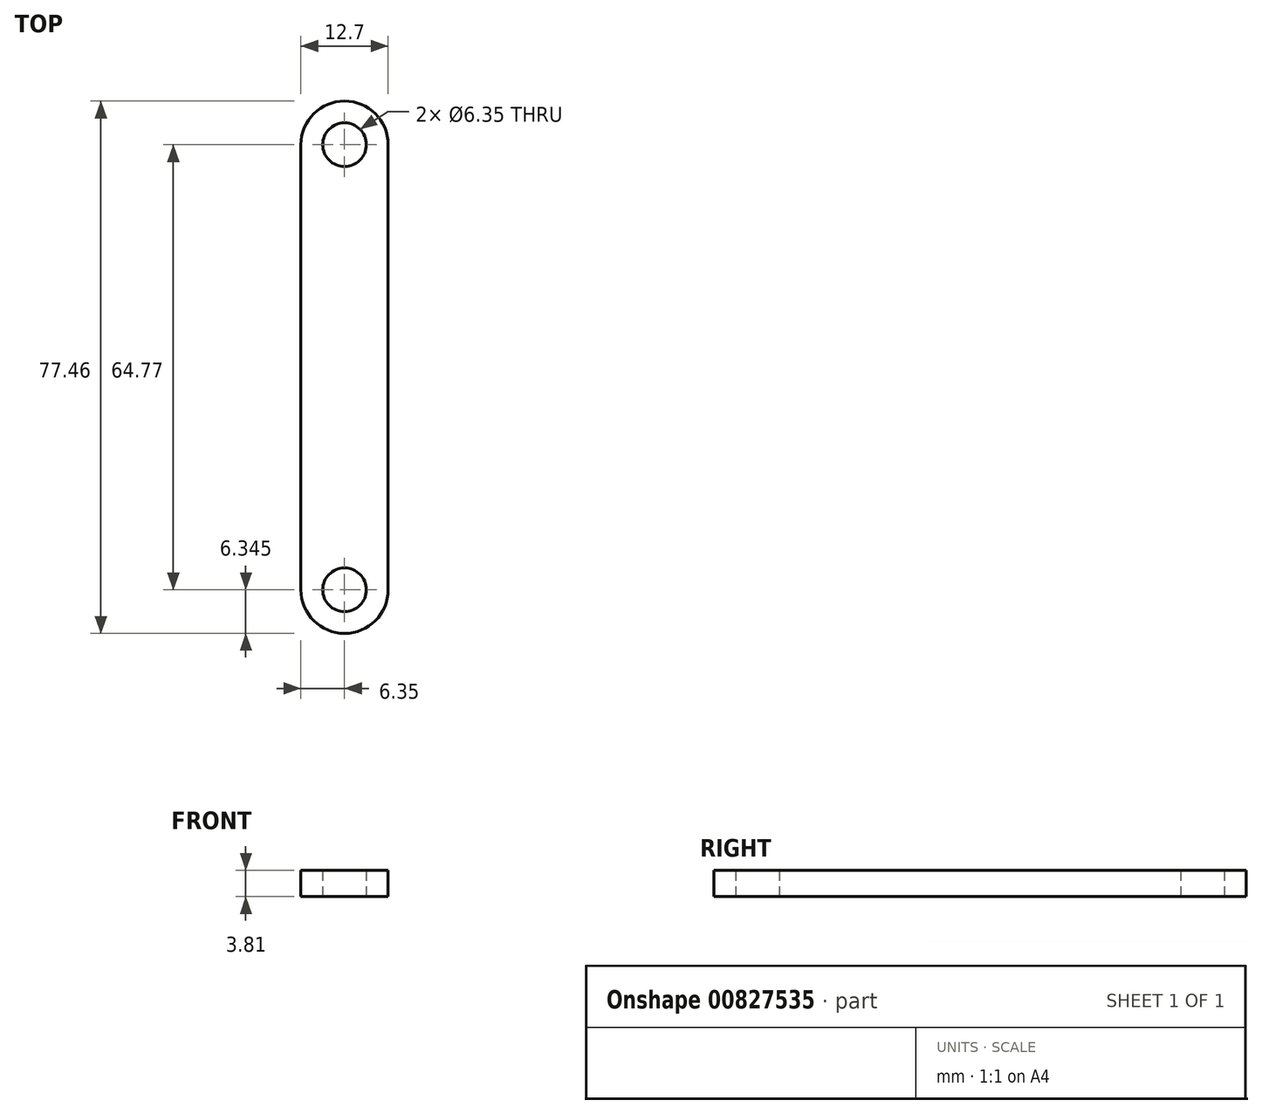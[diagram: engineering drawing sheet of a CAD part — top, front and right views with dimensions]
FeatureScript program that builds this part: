
annotation { "Feature Type Name" : "Feature", "Feature Type Description" : "" }
export const myFeature = defineFeature(function(context is Context, id is Id, definition is map)
    precondition{}
    {
        {
            var Q0;
            Q0=qCreatedBy(makeId("Top.planeOp"),FACE);
            var sketch = newSketch(context, id + "F0", { "sketchPlane" : qUnion([Q0])});
            skCircle(sketch, "E0", {"center": v(0, 32.39) * mm, "radius": 3.18 * mm});
            skCircle(sketch, "E1", {"center": v(0, -32.39) * mm, "radius": 3.18 * mm});
            skLineSegment(sketch, "E2", {"start": v(0, 0) * mm, "end": v(0, 29.21) * mm});
            skLineSegment(sketch, "E3", {"start": v(0, 0) * mm, "end": v(0, -29.21) * mm});
            skLineSegment(sketch, "E4.bottom", {"start": v(-6.35, 32.39) * mm, "end": v(6.35, 32.39) * mm});
            skLineSegment(sketch, "E4.top", {"start": v(-6.35, -32.38) * mm, "end": v(6.35, -32.38) * mm});
            skLineSegment(sketch, "E4.left", {"start": v(-6.35, 32.39) * mm, "end": v(-6.35, -32.39) * mm});
            skLineSegment(sketch, "E4.right", {"start": v(6.35, 32.39) * mm, "end": v(6.35, -32.39) * mm});
            skPoint(sketch, "E4.middle", {"position": v(0, 0) * mm});
            skArc(sketch, "E5", {"start": v(6.35, 32.39) * mm, "mid": v(0, 38.74) * mm, "end": v(-6.35, 32.39) * mm});
            skArc(sketch, "E6.MirrorCS", {"start": v(6.35, -32.39) * mm, "mid": v(0, -38.74) * mm, "end": v(-6.35, -32.39) * mm});
            skSolve(sketch);
        }
        {
            var Q0;
            Q0 = qSketchRegion(id + "F0", true);
            extrude(context, id + "F1", {"entities" : qUnion([Q0]), "depth" : 3.8 * mm, "offsetDistance" : 25.4 * mm});
        }
    });
